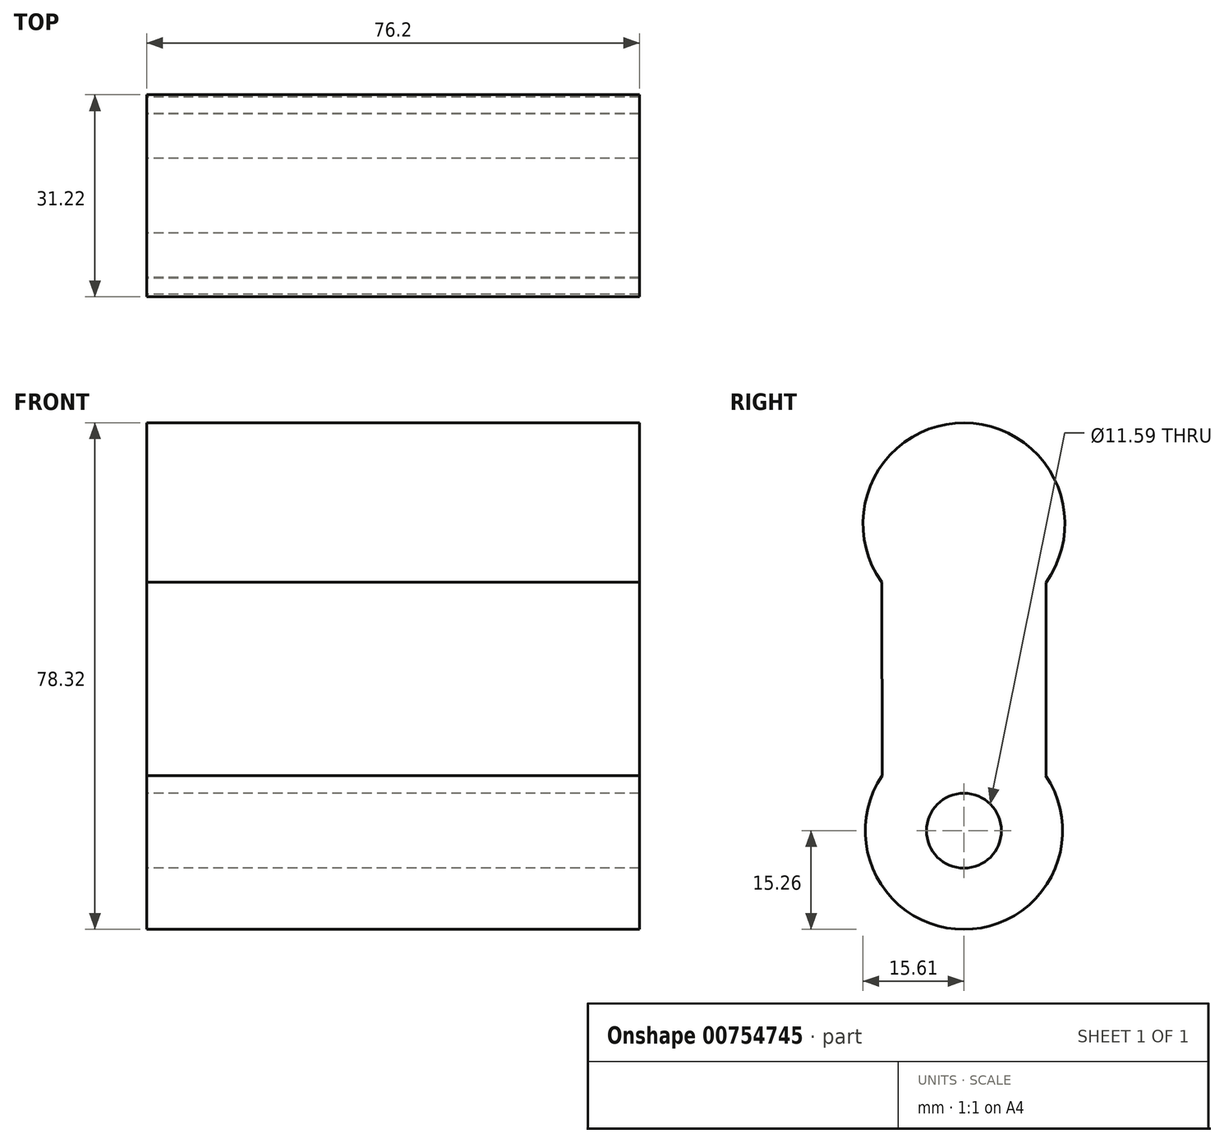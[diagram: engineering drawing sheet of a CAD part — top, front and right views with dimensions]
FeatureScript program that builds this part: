
annotation { "Feature Type Name" : "Feature", "Feature Type Description" : "" }
export const myFeature = defineFeature(function(context is Context, id is Id, definition is map)
    precondition{}
    {
        {
            var Q0;
            Q0=qCreatedBy(makeId("Right.planeOp"),FACE);
            var sketch = newSketch(context, id + "F0", { "sketchPlane" : qUnion([Q0])});
            skCircle(sketch, "E0", {"center": v(0, 0) * mm, "radius": 15.26 * mm});
            skSolve(sketch);
        }
        {
            var Q0;
            Q0=makeQuery(id+"F0.imprint","IMPRINT",FACE,{"disambiguationData":[TD([[makeQuery(id+"F0.imprint","IMPRINT",EDGE,{"derivedFrom":sQuery(id+"F0.wireOp",EDGE,"E0")}),1.0]])]});
            extrude(context, id + "F1", {"entities" : qUnion([Q0]), "depth" : 38.1 * mm, "offsetDistance" : 25.4 * mm});
        }
        {
            var Q0;
            Q0=qCreatedBy(makeId("Right.planeOp"),FACE);
            var sketch = newSketch(context, id + "F2", { "sketchPlane" : qUnion([Q0])});
            skCircle(sketch, "E1", {"center": v(0, 0) * mm, "radius": 15.22 * mm});
            skSolve(sketch);
        }
        {
            var Q0;
            Q0=makeQuery(id+"F2.imprint","IMPRINT",FACE,{"disambiguationData":[TD([[makeQuery(id+"F2.imprint","IMPRINT",EDGE,{"derivedFrom":sQuery(id+"F2.wireOp",EDGE,"E1")}),1.0]])]});
            extrude(context, id + "F3", {"entities" : qUnion([Q0]), "operationType" : NewBodyOperationType.ADD, "depth" : 38.1 * mm, "offsetDistance" : 25.4 * mm});
        }
        {
            var Q0;
            Q0 = qSketchRegion(id + "F2", true);
            extrude(context, id + "F4", {"entities" : qUnion([Q0]), "operationType" : NewBodyOperationType.ADD, "oppositeDirection" : true, "depth" : 38.1 * mm, "offsetDistance" : 25.4 * mm});
        }
        {
            var Q0;
            Q0=qCreatedBy(makeId("Right.planeOp"),FACE);
            var sketch = newSketch(context, id + "F5", { "sketchPlane" : qUnion([Q0])});
            skCircle(sketch, "E2", {"center": v(0, 0) * mm, "radius": 5.8 * mm});
            skSolve(sketch);
        }
        {
            var Q0;
            Q0 = qSketchRegion(id + "F5", true);
            extrude(context, id + "F6", {"entities" : qUnion([Q0]), "operationType" : NewBodyOperationType.ADD, "oppositeDirection" : true, "depth" : 50.8 * mm, "offsetDistance" : 25.4 * mm});
        }
        {
            var Q0;
            Q0=makeQuery(id+"F6.opExtrude","CAP_FACE",FACE,{"disambiguationData":[OSD([sQuery(id+"F5.wireOp",EDGE,"E2")])],"isStart":false});
            extrude(context, id + "F7", {"entities" : qUnion([Q0]), "operationType" : NewBodyOperationType.REMOVE, "oppositeDirection" : true, "depth" : 101.6 * mm, "offsetDistance" : 25.4 * mm});
        }
        {
            var Q0;
            Q0=qCreatedBy(makeId("Front.planeOp"),FACE);
            var sketch = newSketch(context, id + "F8", { "sketchPlane" : qUnion([Q0])});
            skLineSegment(sketch, "E3", {"start": v(-37.9, 0) * mm, "end": v(-28.58, 0) * mm});
            skLineSegment(sketch, "E4", {"start": v(-28.58, 0) * mm, "end": v(-28.58, 38.7) * mm});
            skLineSegment(sketch, "E5", {"start": v(-28.58, 38.7) * mm, "end": v(-37.97, 38.7) * mm});
            skLineSegment(sketch, "E6", {"start": v(-37.97, 38.7) * mm, "end": v(-37.9, 0) * mm});
            skSolve(sketch);
        }
        {
            var Q0;
            Q0=qCreatedBy(makeId("Right.planeOp"),FACE);
            var sketch = newSketch(context, id + "F9", { "sketchPlane" : qUnion([Q0])});
            skLineSegment(sketch, "E7", {"start": v(-12.66, 8.52) * mm, "end": v(12.68, 8.52) * mm});
            skLineSegment(sketch, "E8", {"start": v(12.68, 8.52) * mm, "end": v(12.68, 38.63) * mm});
            skLineSegment(sketch, "E9", {"start": v(12.68, 38.63) * mm, "end": v(-12.73, 38.63) * mm});
            skLineSegment(sketch, "E10", {"start": v(-12.73, 38.63) * mm, "end": v(-12.66, 8.52) * mm});
            skSolve(sketch);
        }
        {
            var Q0;
            Q0=makeQuery(id+"F9.imprint","IMPRINT",FACE,{"disambiguationData":[TD([[makeQuery(id+"F9.imprint","IMPRINT",EDGE,{"derivedFrom":sQuery(id+"F9.wireOp",EDGE,"E7")}),1.0]])]});
            extrude(context, id + "F10", {"entities" : qUnion([Q0]), "operationType" : NewBodyOperationType.ADD, "depth" : 38.1 * mm, "offsetDistance" : 25.4 * mm});
        }
        {
            var Q0;
            Q0=makeQuery(id+"F10.boolean.opBoolean","MERGE",FACE,{"derivedFrom":[makeQuery(id+"F1.opExtrude","CAP_FACE",FACE,{"disambiguationData":[OSD([sQuery(id+"F0.wireOp",EDGE,"E0")])],"isStart":true}),makeQuery(id+"F10.opExtrude","CAP_FACE",FACE,{"disambiguationData":[OSD([sQuery(id+"F9.wireOp",EDGE,"E7"),sQuery(id+"F9.wireOp",EDGE,"E8"),sQuery(id+"F9.wireOp",EDGE,"E9"),sQuery(id+"F9.wireOp",EDGE,"E10")])],"isStart":true})]});
            extrude(context, id + "F11", {"entities" : qUnion([Q0]), "operationType" : NewBodyOperationType.ADD, "depth" : 38.1 * mm, "offsetDistance" : 25.4 * mm});
        }
        {
            var Q0;
            Q0=qCreatedBy(makeId("Right.planeOp"),FACE);
            var sketch = newSketch(context, id + "F12", { "sketchPlane" : qUnion([Q0])});
            skCircle(sketch, "E11", {"center": v(0, 47.46) * mm, "radius": 15.6 * mm});
            skSolve(sketch);
        }
        {
            var Q0;
            Q0=makeQuery(id+"F12.imprint","IMPRINT",FACE,{"disambiguationData":[TD([[makeQuery(id+"F12.imprint","IMPRINT",EDGE,{"derivedFrom":sQuery(id+"F12.wireOp",EDGE,"E11")}),1.0]])]});
            extrude(context, id + "F13", {"entities" : qUnion([Q0]), "operationType" : NewBodyOperationType.ADD, "depth" : 38.1 * mm, "offsetDistance" : 25.4 * mm});
        }
        {
            var Q0;
            Q0=makeQuery(id+"F13.opExtrude","CAP_FACE",FACE,{"disambiguationData":[OSD([sQuery(id+"F12.wireOp",EDGE,"E11")])],"isStart":true});
            extrude(context, id + "F14", {"entities" : qUnion([Q0]), "operationType" : NewBodyOperationType.ADD, "oppositeDirection" : true, "depth" : 38.1 * mm, "offsetDistance" : 25.4 * mm});
        }
        {
            var Q0;
            Q0=makeQuery(id+"F13.opExtrude","CAP_FACE",FACE,{"disambiguationData":[OSD([sQuery(id+"F12.wireOp",EDGE,"E11")])],"isStart":true});
            extrude(context, id + "F15", {"entities" : qUnion([Q0]), "operationType" : NewBodyOperationType.ADD, "depth" : 38.1 * mm, "offsetDistance" : 25.4 * mm});
        }
    });
